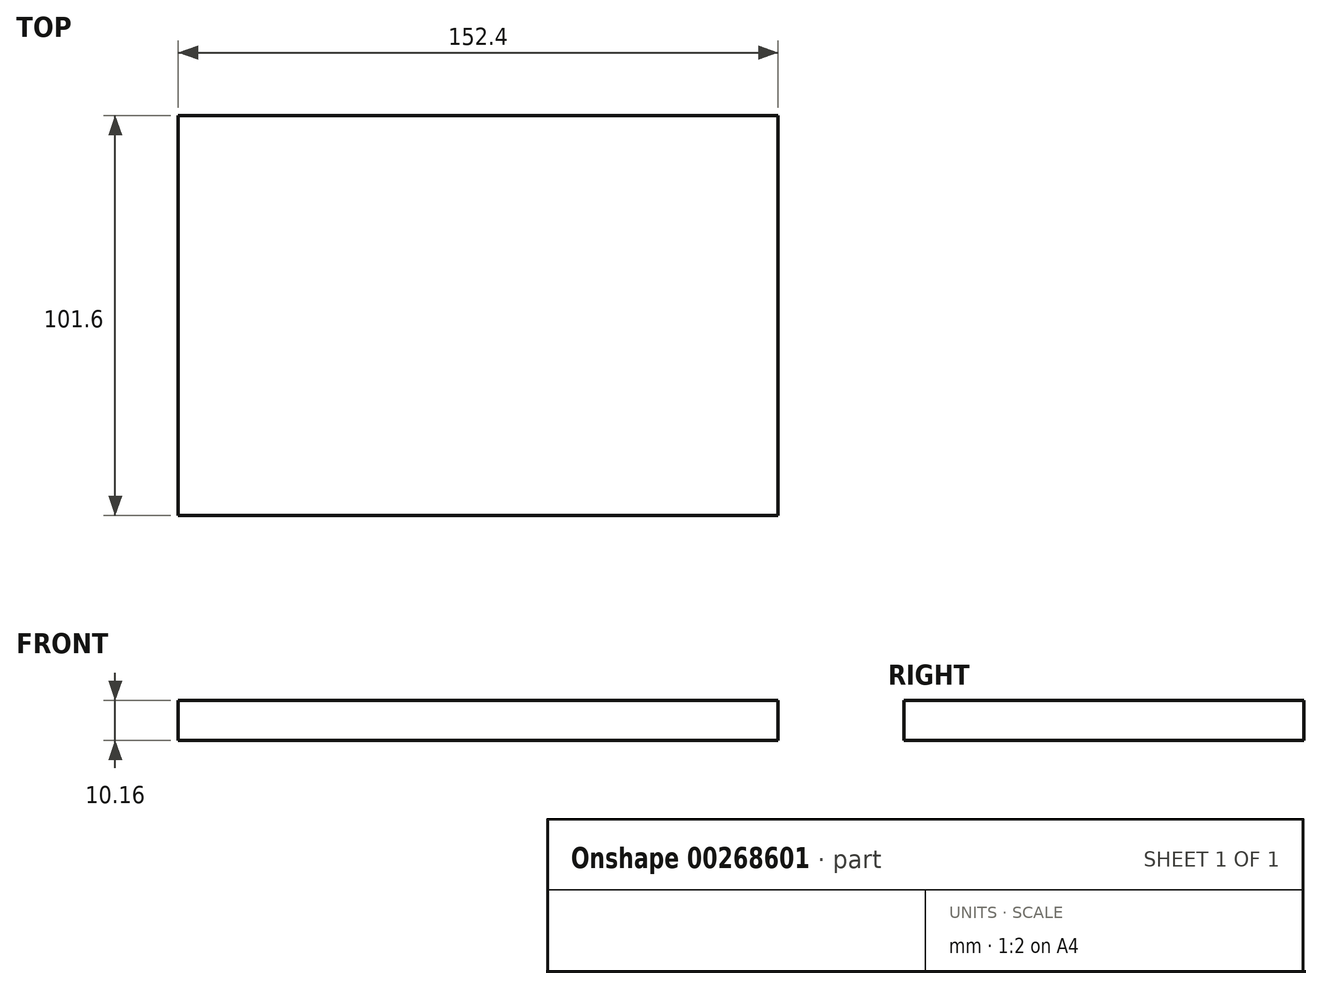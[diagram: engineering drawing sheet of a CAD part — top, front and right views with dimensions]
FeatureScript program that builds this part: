
annotation { "Feature Type Name" : "Feature", "Feature Type Description" : "" }
export const myFeature = defineFeature(function(context is Context, id is Id, definition is map)
    precondition{}
    {
        {
            var Q0;
            Q0=qCreatedBy(makeId("Top.planeOp"),FACE);
            var sketch = newSketch(context, id + "F0", { "sketchPlane" : qUnion([Q0])});
            skLineSegment(sketch, "E0.bottom", {"start": v(-76.2, 50.8) * mm, "end": v(76.2, 50.8) * mm});
            skLineSegment(sketch, "E0.top", {"start": v(-76.2, -50.8) * mm, "end": v(76.2, -50.8) * mm});
            skLineSegment(sketch, "E0.left", {"start": v(-76.2, 50.8) * mm, "end": v(-76.2, -50.8) * mm});
            skLineSegment(sketch, "E0.right", {"start": v(76.2, 50.8) * mm, "end": v(76.2, -50.8) * mm});
            skSolve(sketch);
        }
        {
            var Q0;
            Q0=makeQuery(id+"F0.imprint","IMPRINT",FACE,{"disambiguationData":[TD([[makeQuery(id+"F0.imprint","IMPRINT",EDGE,{"derivedFrom":sQuery(id+"F0.wireOp",EDGE,"E0.bottom")}),-1.0]])]});
            extrude(context, id + "F1", {"entities" : qUnion([Q0]), "depth" : 10.16 * mm, "offsetDistance" : 25.4 * mm});
        }
    });
